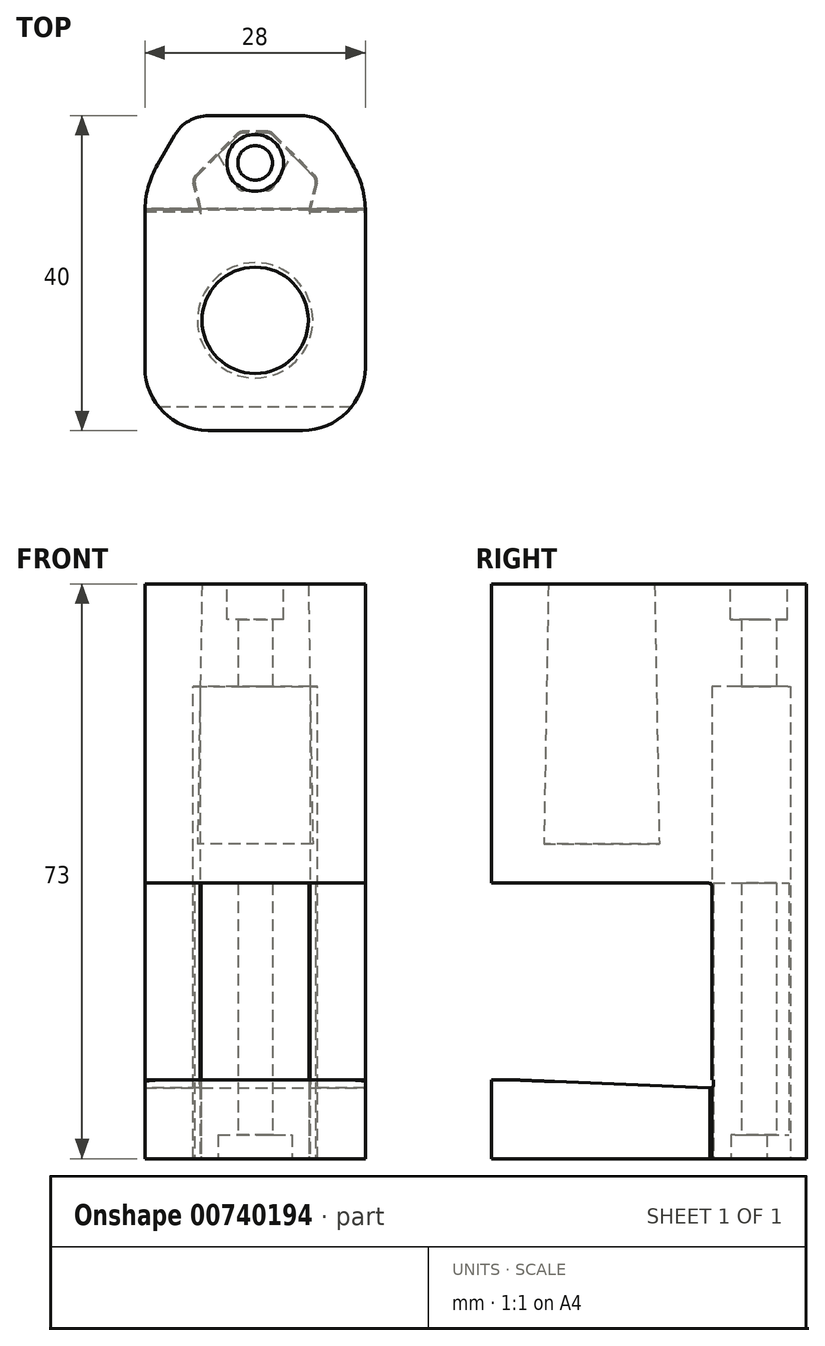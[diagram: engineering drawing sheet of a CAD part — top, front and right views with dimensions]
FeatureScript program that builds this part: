
annotation { "Feature Type Name" : "Feature", "Feature Type Description" : "" }
export const myFeature = defineFeature(function(context is Context, id is Id, definition is map)
    precondition{}
    {
        {
            assignVariable(context, id + "F0", {"name" : "lamppostDepth", "anyValue" : 33});
        }
        {
            var Q0;
            Q0=qCreatedBy(makeId("Right.planeOp"),FACE);
            var sketch = newSketch(context, id + "F1", { "sketchPlane" : qUnion([Q0])});
            skLineSegment(sketch, "E0", {"start": v(0, 0) * mm, "end": v(-28, 0) * mm});
            skLineSegment(sketch, "E1", {"start": v(-28, 0) * mm, "end": v(-28, 38) * mm});
            skLineSegment(sketch, "E2", {"start": v(-28, 38) * mm, "end": v(12, 38) * mm});
            skLineSegment(sketch, "E3", {"start": v(12, 38) * mm, "end": v(12, -35) * mm});
            skLineSegment(sketch, "E4", {"start": v(12, -35) * mm, "end": v(0, -35) * mm});
            skLineSegment(sketch, "E5", {"start": v(0, -35) * mm, "end": v(0, 0) * mm});
            skLineSegment(sketch, "E6", {"start": v(0, -25) * mm, "end": v(-22.92, -25) * mm, "construction": true});
            skSolve(sketch);
        }
        {
            var Q0;
            Q0=qSketchRegion(id+"F1",true);
            extrude(context, id + "F2", {"entities" : qUnion([Q0]), "endBound" : BoundingType.SYMMETRIC, "depth" : 28 * mm, "offsetDistance" : 25 * mm});
        }
        {
            var Q0;
            Q0=makeQuery(id+"F2.opExtrude","SWEPT_FACE",FACE,{"disambiguationData":[OSD([sQuery(id+"F1.wireOp",EDGE,"E2")])]});
            var sketch = newSketch(context, id + "F3", { "sketchPlane" : qUnion([Q0])});
            skCircle(sketch, "E7", {"center": v(0, -14) * mm, "radius": 6.75 * mm});
            skLineSegment(sketch, "E8", {"start": v(14, -28) * mm, "end": v(-14, 0) * mm, "construction": true});
            skLineSegment(sketch, "E9", {"start": v(-14, 0) * mm, "end": v(-14, -28) * mm, "construction": true});
            skSolve(sketch);
        }
        {
            var Q0;
            Q0=qSketchRegion(id+"F3",true);
            extrude(context, id + "F4", {"entities" : qUnion([Q0]), "operationType" : NewBodyOperationType.REMOVE, "oppositeDirection" : true, "depth" : (getVariable(context, 'lamppostDepth')) * mm, "offsetDistance" : 25 * mm, "hasDraft" : true, "draftAngle" : 1 * degree});
        }
        {
            var Q0;
            Q0=makeQuery(id+"F2.opExtrude","SWEPT_FACE",FACE,{"disambiguationData":[OSD([sQuery(id+"F1.wireOp",EDGE,"E4")])]});
            var sketch = newSketch(context, id + "F5", { "sketchPlane" : qUnion([Q0])});
            skCircle(sketch, "E10", {"center": v(0, -6) * mm, "radius": 2.2 * mm});
            skLineSegment(sketch, "E11", {"start": v(-14, -12) * mm, "end": v(14, 0) * mm, "construction": true});
            skSolve(sketch);
        }
        {
            var Q0;
            Q0=qSketchRegion(id+"F5",true);
            extrude(context, id + "F6", {"entities" : qUnion([Q0]), "operationType" : NewBodyOperationType.REMOVE, "endBound" : BoundingType.THROUGH_ALL, "oppositeDirection" : true, "depth" : 25 * mm, "offsetDistance" : 25 * mm});
        }
        {
            var Q0;
            Q0=makeQuery(id+"F2.opExtrude","SWEPT_FACE",FACE,{"disambiguationData":[OSD([sQuery(id+"F1.wireOp",EDGE,"E2")])]});
            var sketch = newSketch(context, id + "F7", { "sketchPlane" : qUnion([Q0])});
            skCircle(sketch, "E12", {"center": v(0, 6) * mm, "radius": 3.6 * mm});
            skSolve(sketch);
        }
        {
            var Q0;
            Q0=qSketchRegion(id+"F7",true);
            extrude(context, id + "F8", {"entities" : qUnion([Q0]), "operationType" : NewBodyOperationType.REMOVE, "oppositeDirection" : true, "depth" : 4.5 * mm, "offsetDistance" : 25 * mm});
        }
        {
            var Q0;
            Q0=makeQuery(id+"F2.opExtrude","SWEPT_FACE",FACE,{"disambiguationData":[OSD([sQuery(id+"F1.wireOp",EDGE,"E4")])]});
            var sketch = newSketch(context, id + "F9", { "sketchPlane" : qUnion([Q0])});
            skLineSegment(sketch, "E13", {"start": v(2, -10) * mm, "end": v(-2, -10) * mm});
            skPoint(sketch, "E14", {"position": v(0, -6) * mm});
            skLineSegment(sketch, "E15", {"start": v(0, -6) * mm, "end": v(0, -10) * mm, "construction": true});
            skLineSegment(sketch, "E16", {"start": v(2, -10) * mm, "end": v(8, -4) * mm});
            skLineSegment(sketch, "E17", {"start": v(8, -4) * mm, "end": v(7, 0) * mm});
            skLineSegment(sketch, "E18", {"start": v(7, 0) * mm, "end": v(-7, 0) * mm});
            skLineSegment(sketch, "E19", {"start": v(-7, 0) * mm, "end": v(-8, -4) * mm});
            skLineSegment(sketch, "E20", {"start": v(-8, -4) * mm, "end": v(-2, -10) * mm});
            skSolve(sketch);
        }
        {
            var Q0;
            Q0=qSketchRegion(id+"F9",true);
            extrude(context, id + "F10", {"entities" : qUnion([Q0]), "operationType" : NewBodyOperationType.REMOVE, "oppositeDirection" : true, "depth" : 60 * mm, "offsetDistance" : 25 * mm});
        }
        {
            var Q0;
            Q0=makeQuery(id+"F2.opExtrude","SWEPT_FACE",FACE,{"disambiguationData":[OSD([sQuery(id+"F1.wireOp",EDGE,"E4")])]});
            var sketch = newSketch(context, id + "F11", { "sketchPlane" : qUnion([Q0])});
            skLineSegment(sketch, "E21.0", {"start": v(7.78, -3.94) * mm, "end": v(6.84, -0.2) * mm});
            skLineSegment(sketch, "E21.1", {"start": v(-6.84, -0.2) * mm, "end": v(-7.78, -3.94) * mm});
            skLineSegment(sketch, "E21.2", {"start": v(-7.78, -3.94) * mm, "end": v(-1.92, -9.8) * mm});
            skLineSegment(sketch, "E21.3", {"start": v(1.92, -9.8) * mm, "end": v(-1.92, -9.8) * mm});
            skLineSegment(sketch, "E21.4", {"start": v(1.92, -9.8) * mm, "end": v(7.78, -3.94) * mm});
            skLineSegment(sketch, "E22", {"start": v(6.84, -0.2) * mm, "end": v(-6.84, -0.2) * mm});
            skCircle(sketch, "E23.0", {"center": v(0, -6) * mm, "radius": 2.2 * mm});
            skSolve(sketch);
        }
        {
            var Q0;
            Q0=qSketchRegion(id+"F11",true);
            extrude(context, id + "F12", {"entities" : qUnion([Q0]), "oppositeDirection" : true, "depth" : 35 * mm, "offsetDistance" : 25 * mm});
        }
        {
            var Q0;
            Q0=makeQuery(id+"F12.opExtrude","CAP_FACE",FACE,{"disambiguationData":[OSD([sQuery(id+"F11.wireOp",EDGE,"E21.0"),sQuery(id+"F11.wireOp",EDGE,"E21.1"),sQuery(id+"F11.wireOp",EDGE,"E21.2"),sQuery(id+"F11.wireOp",EDGE,"E21.3"),sQuery(id+"F11.wireOp",EDGE,"E21.4"),sQuery(id+"F11.wireOp",EDGE,"E22"),sQuery(id+"F11.wireOp",EDGE,"E23.0")])],"isStart":true});
            var sketch = newSketch(context, id + "F13", { "sketchPlane" : qUnion([Q0])});
            skLineSegment(sketch, "E24", {"start": v(14, 28) * mm, "end": v(-14, 28) * mm});
            skLineSegment(sketch, "E25", {"start": v(-14, 28) * mm, "end": v(-14, 0.2) * mm});
            skLineSegment(sketch, "E26", {"start": v(-14, 0.2) * mm, "end": v(-6.84, 0.2) * mm});
            skLineSegment(sketch, "E27", {"start": v(-6.84, 0.2) * mm, "end": v(-6.84, -0.2) * mm});
            skLineSegment(sketch, "E28", {"start": v(-6.84, -0.2) * mm, "end": v(6.84, -0.2) * mm});
            skLineSegment(sketch, "E29", {"start": v(6.84, -0.2) * mm, "end": v(6.84, 0.2) * mm});
            skLineSegment(sketch, "E30", {"start": v(6.84, 0.2) * mm, "end": v(14, 0.2) * mm});
            skLineSegment(sketch, "E31", {"start": v(14, 0.2) * mm, "end": v(14, 28) * mm});
            skSolve(sketch);
        }
        {
            var Q0;
            Q0=makeQuery(id+"F13.imprint","IMPRINT",FACE,{"disambiguationData":[TD([[makeQuery(id+"F13.imprint","IMPRINT",EDGE,{"derivedFrom":sQuery(id+"F13.wireOp",EDGE,"E24")}),1.0]])]});
            var Q1;
            Q1=sQuery(id+"F1.wireOp",VERTEX,"E6.end");
            extrude(context, id + "F14", {"entities" : qUnion([Q0]), "operationType" : NewBodyOperationType.ADD, "endBound" : BoundingType.UP_TO_VERTEX, "oppositeDirection" : true, "depth" : 10 * mm, "endBoundEntityVertex" : qUnion([Q1]), "offsetDistance" : 25 * mm});
        }
        {
            var Q0;
            Q0=makeQuery(id+"F14.boolean.opBoolean","MERGE",FACE,{"derivedFrom":[makeQuery(id+"F12.opExtrude","CAP_FACE",FACE,{"disambiguationData":[OSD([sQuery(id+"F11.wireOp",EDGE,"E21.0"),sQuery(id+"F11.wireOp",EDGE,"E21.1"),sQuery(id+"F11.wireOp",EDGE,"E21.2"),sQuery(id+"F11.wireOp",EDGE,"E21.3"),sQuery(id+"F11.wireOp",EDGE,"E21.4"),sQuery(id+"F11.wireOp",EDGE,"E22"),sQuery(id+"F11.wireOp",EDGE,"E23.0")])],"isStart":true}),makeQuery(id+"F14.opExtrude","CAP_FACE",FACE,{"disambiguationData":[OSD([sQuery(id+"F13.wireOp",EDGE,"E24"),sQuery(id+"F13.wireOp",EDGE,"E25"),sQuery(id+"F13.wireOp",EDGE,"E26"),sQuery(id+"F13.wireOp",EDGE,"E27"),sQuery(id+"F13.wireOp",EDGE,"E28"),sQuery(id+"F13.wireOp",EDGE,"E29"),sQuery(id+"F13.wireOp",EDGE,"E30"),sQuery(id+"F13.wireOp",EDGE,"E31")])],"isStart":true})]});
            var sketch = newSketch(context, id + "F15", { "sketchPlane" : qUnion([Q0])});
            skCircle(sketch, "E32", {"center": v(0, -6) * mm, "radius": 4.1 * mm, "construction": true});
            skLineSegment(sketch, "E33", {"start": v(2.05, -2.45) * mm, "end": v(-2.05, -2.45) * mm});
            skLineSegment(sketch, "E34", {"start": v(2.05, -2.45) * mm, "end": v(4.1, -6) * mm});
            skLineSegment(sketch, "E35", {"start": v(4.1, -6) * mm, "end": v(0, -6) * mm, "construction": true});
            skLineSegment(sketch, "E36", {"start": v(0, -6) * mm, "end": v(-4.1, -6) * mm, "construction": true});
            skLineSegment(sketch, "E37", {"start": v(-4.1, -6) * mm, "end": v(-2.05, -2.45) * mm});
            skLineSegment(sketch, "E38", {"start": v(4.1, -6) * mm, "end": v(4.7, -7.03) * mm});
            skLineSegment(sketch, "E39", {"start": v(4.7, -7.03) * mm, "end": v(1.92, -9.8) * mm});
            skLineSegment(sketch, "E40", {"start": v(1.92, -9.8) * mm, "end": v(-1.92, -9.8) * mm});
            skLineSegment(sketch, "E41", {"start": v(-1.92, -9.8) * mm, "end": v(-4.7, -7.03) * mm});
            skLineSegment(sketch, "E42", {"start": v(-4.7, -7.03) * mm, "end": v(-4.1, -6) * mm});
            skSolve(sketch);
        }
        {
            var Q0;
            Q0=qSketchRegion(id+"F15",true);
            extrude(context, id + "F16", {"entities" : qUnion([Q0]), "operationType" : NewBodyOperationType.REMOVE, "oppositeDirection" : true, "depth" : 3 * mm, "offsetDistance" : 25 * mm});
        }
        {
            var Q0;
            Q0=makeQuery(id+"F2.opExtrude","CAP_EDGE",EDGE,{"disambiguationData":[OSD([sQuery(id+"F1.wireOp",EDGE,"E1")])],"isStart":false});
            var Q1;
            Q1=makeQuery(id+"F2.opExtrude","CAP_EDGE",EDGE,{"disambiguationData":[OSD([sQuery(id+"F1.wireOp",EDGE,"E1")])],"isStart":true});
            var Q2;
            Q2=makeQuery(id+"F14.opExtrude","SWEPT_EDGE",EDGE,{"disambiguationData":[OSD([sQuery(id+"F13.wireOp",EDGE,"E24"),sQuery(id+"F13.wireOp",EDGE,"E31")])]});
            var Q3;
            Q3=makeQuery(id+"F14.opExtrude","SWEPT_EDGE",EDGE,{"disambiguationData":[OSD([sQuery(id+"F13.wireOp",EDGE,"E24"),sQuery(id+"F13.wireOp",EDGE,"E25")])]});
            fillet(context, id + "F17", {"entities" : qUnion([Q0, Q1, Q2, Q3]), "radius" : 8 * mm, "tangentPropagation" : true, "allowEdgeOverflow" : false});
        }
        {
            var Q0;
            Q0=makeQuery(id+"F2.opExtrude","CAP_EDGE",EDGE,{"disambiguationData":[OSD([sQuery(id+"F1.wireOp",EDGE,"E3")])],"isStart":true});
            var Q1;
            Q1=makeQuery(id+"F2.opExtrude","CAP_EDGE",EDGE,{"disambiguationData":[OSD([sQuery(id+"F1.wireOp",EDGE,"E3")])],"isStart":false});
            chamfer(context, id + "F18", {"entities" : qUnion([Q0, Q1]), "chamferType" : ChamferType.OFFSET_ANGLE, "width" : 9 * mm, "oppositeDirection" : false, "angle" : 30 * degree, "tangentPropagation" : true});
        }
        {
            var Q0;
            {var subQ0=sQuery(id+"F1.wireOp",EDGE,"E3");Q0=makeQuery(id+"F18.opChamfer","BLEND_EDGE",EDGE,{"blendedFrom":[makeQuery(id+"F2.opExtrude","CAP_EDGE",EDGE,{"disambiguationData":[OSD([subQ0])],"isStart":true}),makeQuery(id+"F2.opExtrude","CAP_FACE",FACE,{"disambiguationData":[OSD([sQuery(id+"F1.wireOp",EDGE,"E0"),sQuery(id+"F1.wireOp",EDGE,"E1"),sQuery(id+"F1.wireOp",EDGE,"E2"),subQ0,sQuery(id+"F1.wireOp",EDGE,"E4"),sQuery(id+"F1.wireOp",EDGE,"E5")])],"isStart":true})],"blendedInto":[makeQuery(id+"F2.opExtrude","CAP_FACE",FACE,{"disambiguationData":[OSD([sQuery(id+"F1.wireOp",EDGE,"E0"),sQuery(id+"F1.wireOp",EDGE,"E1"),sQuery(id+"F1.wireOp",EDGE,"E2"),subQ0,sQuery(id+"F1.wireOp",EDGE,"E4"),sQuery(id+"F1.wireOp",EDGE,"E5")])],"isStart":true})]});}
            var Q1;
            {var subQ0=sQuery(id+"F1.wireOp",EDGE,"E3");Q1=makeQuery(id+"F18.opChamfer","BLEND_EDGE",EDGE,{"blendedFrom":[makeQuery(id+"F2.opExtrude","CAP_EDGE",EDGE,{"disambiguationData":[OSD([subQ0])],"isStart":false}),makeQuery(id+"F2.opExtrude","CAP_FACE",FACE,{"disambiguationData":[OSD([sQuery(id+"F1.wireOp",EDGE,"E0"),sQuery(id+"F1.wireOp",EDGE,"E1"),sQuery(id+"F1.wireOp",EDGE,"E2"),subQ0,sQuery(id+"F1.wireOp",EDGE,"E4"),sQuery(id+"F1.wireOp",EDGE,"E5")])],"isStart":false})],"blendedInto":[makeQuery(id+"F2.opExtrude","CAP_FACE",FACE,{"disambiguationData":[OSD([sQuery(id+"F1.wireOp",EDGE,"E0"),sQuery(id+"F1.wireOp",EDGE,"E1"),sQuery(id+"F1.wireOp",EDGE,"E2"),subQ0,sQuery(id+"F1.wireOp",EDGE,"E4"),sQuery(id+"F1.wireOp",EDGE,"E5")])],"isStart":false})]});}
            fillet(context, id + "F19", {"entities" : qUnion([Q0, Q1]), "radius" : 12 * mm, "tangentPropagation" : true, "allowEdgeOverflow" : false});
        }
        {
            var Q0;
            {var subQ0=sQuery(id+"F1.wireOp",EDGE,"E3");Q0=makeQuery(id+"F18.opChamfer","BLEND_EDGE",EDGE,{"blendedFrom":[makeQuery(id+"F2.opExtrude","CAP_EDGE",EDGE,{"disambiguationData":[OSD([subQ0])],"isStart":true}),makeQuery(id+"F2.opExtrude","SWEPT_FACE",FACE,{"disambiguationData":[OSD([subQ0])]})],"blendedInto":[makeQuery(id+"F2.opExtrude","SWEPT_FACE",FACE,{"disambiguationData":[OSD([subQ0])]})]});}
            var Q1;
            {var subQ0=sQuery(id+"F1.wireOp",EDGE,"E3");Q1=makeQuery(id+"F18.opChamfer","BLEND_EDGE",EDGE,{"blendedFrom":[makeQuery(id+"F2.opExtrude","CAP_EDGE",EDGE,{"disambiguationData":[OSD([subQ0])],"isStart":false}),makeQuery(id+"F2.opExtrude","SWEPT_FACE",FACE,{"disambiguationData":[OSD([subQ0])]})],"blendedInto":[makeQuery(id+"F2.opExtrude","SWEPT_FACE",FACE,{"disambiguationData":[OSD([subQ0])]})]});}
            fillet(context, id + "F20", {"entities" : qUnion([Q0, Q1]), "radius" : 5 * mm, "tangentPropagation" : true, "allowEdgeOverflow" : false});
        }
        {
            var Q0;
            Q0=makeQuery(id+"F14.opExtrude","SWEPT_FACE",FACE,{"disambiguationData":[OSD([sQuery(id+"F13.wireOp",EDGE,"E25")])]});
            var sketch = newSketch(context, id + "F21", { "sketchPlane" : qUnion([Q0])});
            skLineSegment(sketch, "E43", {"start": v(-0.2, -25) * mm, "end": v(25, -25) * mm});
            skLineSegment(sketch, "E44", {"start": v(25, -25) * mm, "end": v(-0.2, -26) * mm});
            skLineSegment(sketch, "E45", {"start": v(-0.2, -26) * mm, "end": v(-0.2, -25) * mm});
            skSolve(sketch);
        }
        {
            var Q0;
            Q0=qSketchRegion(id+"F21",true);
            extrude(context, id + "F22", {"entities" : qUnion([Q0]), "operationType" : NewBodyOperationType.REMOVE, "endBound" : BoundingType.THROUGH_ALL, "oppositeDirection" : true, "depth" : 25 * mm, "offsetDistance" : 25 * mm});
        }
        {
            var Q0;
            Q0=makeQuery(id+"F14.opExtrude","CAP_EDGE",EDGE,{"disambiguationData":[OSD([sQuery(id+"F13.wireOp",EDGE,"E28")])],"isStart":false});
            var Q1;
            {var subQ0=sQuery(id+"F1.wireOp",EDGE,"E5");var subQ1=makeQuery(id+"F2.opExtrude","SWEPT_FACE",FACE,{"disambiguationData":[OSD([subQ0])]});var subQ2=sQuery(id+"F1.wireOp",EDGE,"E0");var subQ3=makeQuery(id+"F2.opExtrude","SWEPT_FACE",FACE,{"disambiguationData":[OSD([subQ2])]});Q1=makeQuery(id+"F10.boolean.opBoolean","SPLIT",EDGE,{"disambiguationData":[topologyDisambiguationEdgeConnected([subQ3,subQ1]),TD([makeQuery(id+"F10.opExtrude","SWEPT_FACE",FACE,{"disambiguationData":[OSD([sQuery(id+"F9.wireOp",EDGE,"E17")])]})])],"derivedFrom":makeQuery(id+"F2.opExtrude","SWEPT_EDGE",EDGE,{"disambiguationData":[OSD([subQ2,subQ0])]})});}
            var Q2;
            {var subQ0=sQuery(id+"F1.wireOp",EDGE,"E5");var subQ1=makeQuery(id+"F2.opExtrude","SWEPT_FACE",FACE,{"disambiguationData":[OSD([subQ0])]});var subQ2=sQuery(id+"F1.wireOp",EDGE,"E0");var subQ3=makeQuery(id+"F2.opExtrude","SWEPT_FACE",FACE,{"disambiguationData":[OSD([subQ2])]});Q2=makeQuery(id+"F10.boolean.opBoolean","SPLIT",EDGE,{"disambiguationData":[topologyDisambiguationEdgeConnected([subQ3,subQ1]),TD([makeQuery(id+"F10.opExtrude","SWEPT_FACE",FACE,{"disambiguationData":[OSD([sQuery(id+"F9.wireOp",EDGE,"E19")])]})])],"derivedFrom":makeQuery(id+"F2.opExtrude","SWEPT_EDGE",EDGE,{"disambiguationData":[OSD([subQ2,subQ0])]})});}
            var Q3;
            Q3=makeQuery(id+"F22.boolean.opBoolean","COPY",EDGE,{"derivedFrom":makeQuery(id+"F22.opExtrude","SWEPT_EDGE",EDGE,{"disambiguationData":[OSD([sQuery(id+"F21.wireOp",EDGE,"E44"),sQuery(id+"F21.wireOp",EDGE,"E45")])]})});
            fillet(context, id + "F23", {"entities" : qUnion([Q0, Q1, Q2, Q3]), "radius" : .5 * mm, "tangentPropagation" : true, "rho" : .7, "crossSection" : FilletCrossSection.CONIC, "allowEdgeOverflow" : false});
        }
        {
            var Q0;
            Q0=makeQuery(id+"F10.boolean.opBoolean","COPY",EDGE,{"derivedFrom":makeQuery(id+"F10.opExtrude","SWEPT_EDGE",EDGE,{"disambiguationData":[OSD([sQuery(id+"F9.wireOp",EDGE,"E19"),sQuery(id+"F9.wireOp",EDGE,"E20")])]})});
            var Q1;
            Q1=makeQuery(id+"F12.opExtrude","SWEPT_EDGE",EDGE,{"disambiguationData":[OSD([sQuery(id+"F11.wireOp",EDGE,"E21.1"),sQuery(id+"F11.wireOp",EDGE,"E21.2")])]});
            var Q2;
            Q2=makeQuery(id+"F16.boolean.opBoolean","COPY",EDGE,{"derivedFrom":makeQuery(id+"F16.opExtrude","SWEPT_EDGE",EDGE,{"disambiguationData":[OSD([sQuery(id+"F15.wireOp",EDGE,"E33"),sQuery(id+"F15.wireOp",EDGE,"E37")])]})});
            var Q3;
            Q3=makeQuery(id+"F16.boolean.opBoolean","COPY",EDGE,{"derivedFrom":makeQuery(id+"F16.opExtrude","SWEPT_EDGE",EDGE,{"disambiguationData":[OSD([sQuery(id+"F15.wireOp",EDGE,"E33"),sQuery(id+"F15.wireOp",EDGE,"E34")])]})});
            var Q4;
            Q4=makeQuery(id+"F10.boolean.opBoolean","COPY",EDGE,{"derivedFrom":makeQuery(id+"F10.opExtrude","SWEPT_EDGE",EDGE,{"disambiguationData":[OSD([sQuery(id+"F9.wireOp",EDGE,"E13"),sQuery(id+"F9.wireOp",EDGE,"E20")])]})});
            var Q5;
            Q5=makeQuery(id+"F10.boolean.opBoolean","COPY",EDGE,{"derivedFrom":makeQuery(id+"F10.opExtrude","SWEPT_EDGE",EDGE,{"disambiguationData":[OSD([sQuery(id+"F9.wireOp",EDGE,"E13"),sQuery(id+"F9.wireOp",EDGE,"E16")])]})});
            var Q6;
            Q6=makeQuery(id+"F10.boolean.opBoolean","COPY",EDGE,{"derivedFrom":makeQuery(id+"F10.opExtrude","SWEPT_EDGE",EDGE,{"disambiguationData":[OSD([sQuery(id+"F9.wireOp",EDGE,"E16"),sQuery(id+"F9.wireOp",EDGE,"E17")])]})});
            var Q7;
            Q7=makeQuery(id+"F12.opExtrude","SWEPT_EDGE",EDGE,{"disambiguationData":[OSD([sQuery(id+"F11.wireOp",EDGE,"E21.0"),sQuery(id+"F11.wireOp",EDGE,"E21.4")])]});
            var Q8;
            Q8=makeQuery(id+"F12.opExtrude","SWEPT_EDGE",EDGE,{"disambiguationData":[OSD([sQuery(id+"F11.wireOp",EDGE,"E21.3"),sQuery(id+"F11.wireOp",EDGE,"E21.4")])]});
            var Q9;
            Q9=makeQuery(id+"F12.opExtrude","SWEPT_EDGE",EDGE,{"disambiguationData":[OSD([sQuery(id+"F11.wireOp",EDGE,"E21.2"),sQuery(id+"F11.wireOp",EDGE,"E21.3")])]});
            fillet(context, id + "F24", {"entities" : qUnion([Q0, Q1, Q2, Q3, Q4, Q5, Q6, Q7, Q8, Q9]), "radius" : 1 * mm, "tangentPropagation" : true, "allowEdgeOverflow" : false});
        }
    });
